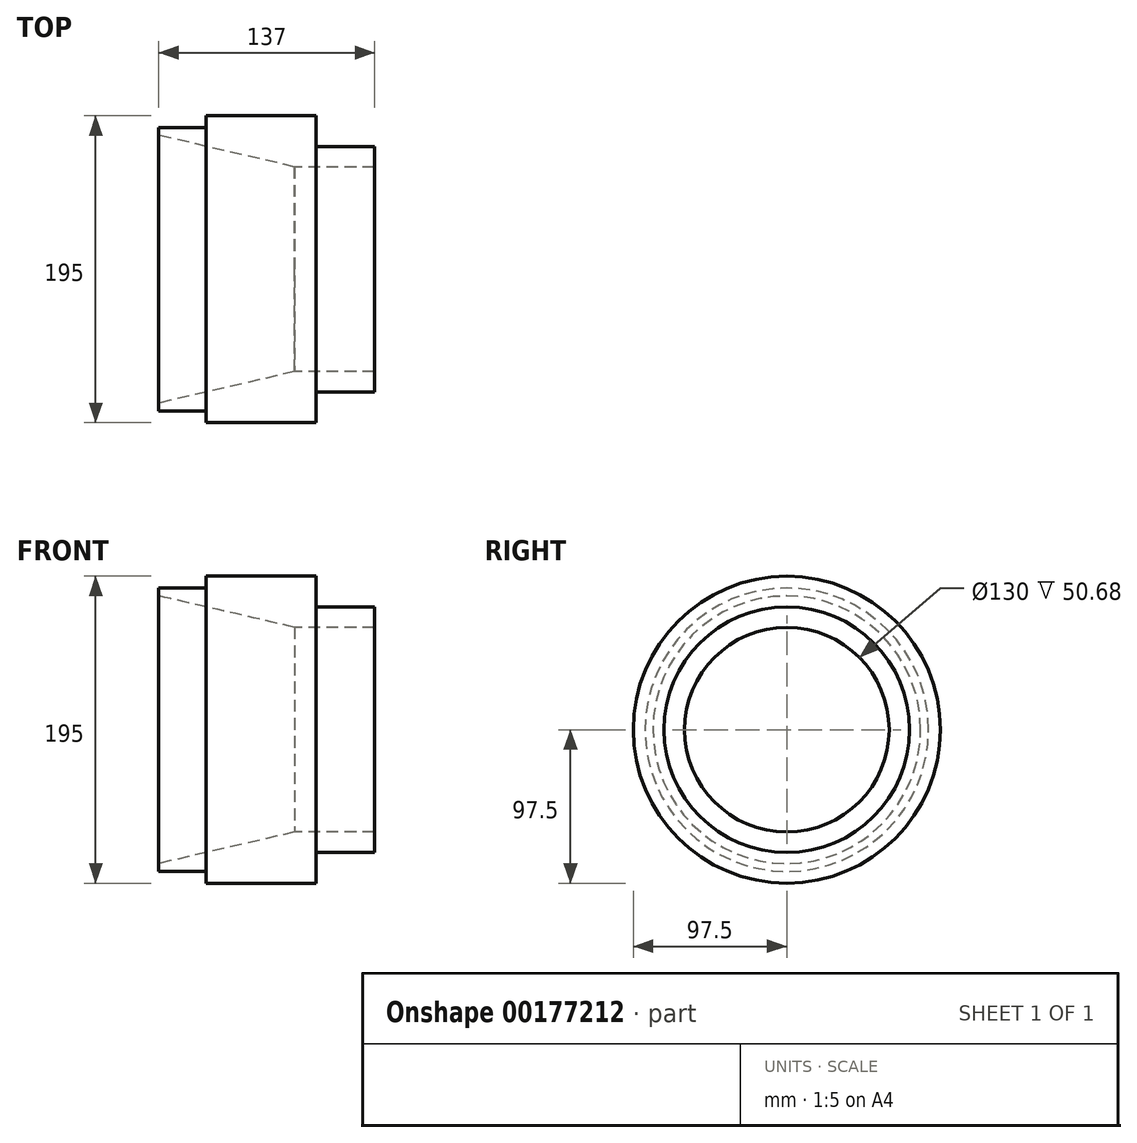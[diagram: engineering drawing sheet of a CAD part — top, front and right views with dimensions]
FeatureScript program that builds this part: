
annotation { "Feature Type Name" : "Feature", "Feature Type Description" : "" }
export const myFeature = defineFeature(function(context is Context, id is Id, definition is map)
    precondition{}
    {
        {
            var Q0;
            Q0=qCreatedBy(makeId("Front.planeOp"),FACE);
            var sketch = newSketch(context, id + "F0", { "sketchPlane" : qUnion([Q0])});
            skLineSegment(sketch, "E0", {"start": v(-95.27, 0) * mm, "end": v(96.4, 0) * mm, "construction": true});
            skLineSegment(sketch, "E1", {"start": v(37, 78) * mm, "end": v(37, 65) * mm});
            skLineSegment(sketch, "E2", {"start": v(37, 65) * mm, "end": v(-13.68, 65) * mm});
            skLineSegment(sketch, "E3", {"start": v(37, 78) * mm, "end": v(0, 78) * mm});
            skLineSegment(sketch, "E4", {"start": v(-13.68, 65) * mm, "end": v(-100, 85) * mm});
            skLineSegment(sketch, "E5", {"start": v(-100, 85) * mm, "end": v(-100, 90) * mm});
            skLineSegment(sketch, "E6", {"start": v(-100, 90) * mm, "end": v(-70, 90) * mm});
            skLineSegment(sketch, "E7", {"start": v(-70, 90) * mm, "end": v(-70, 97.5) * mm});
            skLineSegment(sketch, "E8", {"start": v(-70, 97.5) * mm, "end": v(0, 97.5) * mm});
            skLineSegment(sketch, "E9", {"start": v(0, 97.5) * mm, "end": v(0, 78) * mm});
            skSolve(sketch);
        }
        {
            var Q0;
            Q0=makeQuery(id+"F0.imprint","IMPRINT",FACE,{"disambiguationData":[TD([[makeQuery(id+"F0.imprint","IMPRINT",EDGE,{"derivedFrom":sQuery(id+"F0.wireOp",EDGE,"E1")}),-1.0]])]});
            var Q1;
            Q1=sQuery(id+"F0.wireOp",EDGE,"E0");
            revolve(context, id + "F1", {"entities" : qUnion([Q0]), "axis" : qUnion([Q1]), "revolveType" : RevolveType.FULL});
        }
    });
